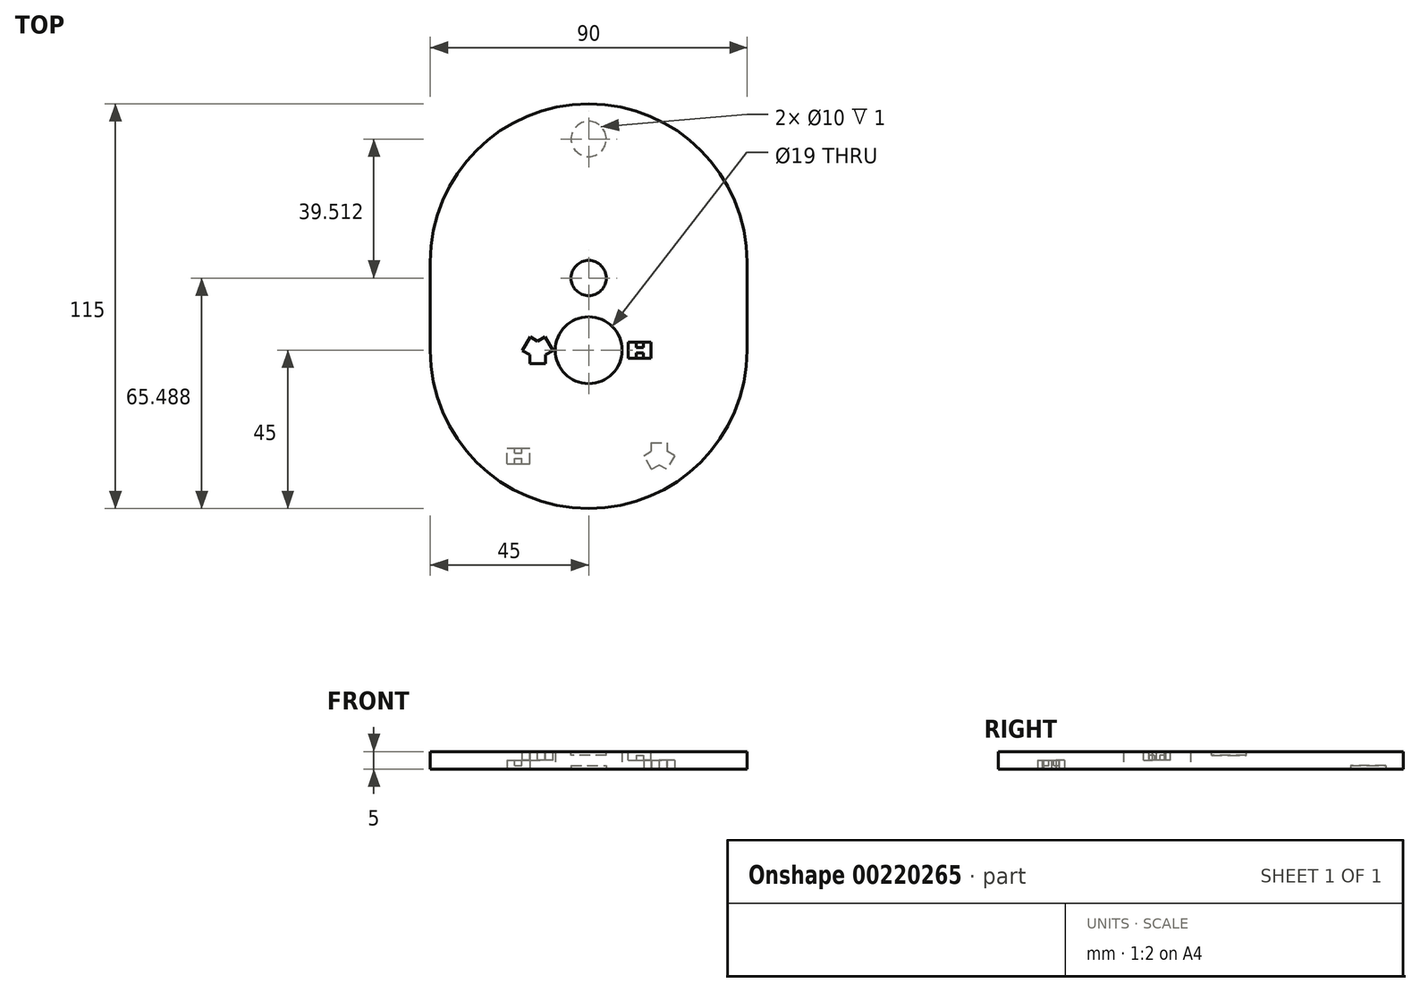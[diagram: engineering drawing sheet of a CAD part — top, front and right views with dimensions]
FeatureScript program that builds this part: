
annotation { "Feature Type Name" : "Feature", "Feature Type Description" : "" }
export const myFeature = defineFeature(function(context is Context, id is Id, definition is map)
    precondition{}
    {
        {
            var Q0;
            Q0=qCreatedBy(makeId("Top.planeOp"),FACE);
            var sketch = newSketch(context, id + "F0", { "sketchPlane" : qUnion([Q0])});
            skArc(sketch, "E0", {"start": v(-45, 0) * mm, "mid": v(0, -45) * mm, "end": v(45, 0) * mm});
            skLineSegment(sketch, "E1", {"start": v(-45, 0) * mm, "end": v(-45, 70) * mm});
            skLineSegment(sketch, "E2", {"start": v(-45, 70) * mm, "end": v(45, 70) * mm});
            skLineSegment(sketch, "E3", {"start": v(45, 70) * mm, "end": v(45, 0) * mm});
            skSolve(sketch);
        }
        {
            var Q0;
            Q0=qSketchRegion(id+"F0",true);
            extrude(context, id + "F1", {"entities" : qUnion([Q0]), "depth" : 5 * mm});
        }
        {
            var Q0;
            Q0=makeQuery(id+"F1.opExtrude","CAP_FACE",FACE,{"disambiguationData":[OSD([sQuery(id+"F0.wireOp",EDGE,"E0")])],"isStart":false});
            var sketch = newSketch(context, id + "F2", { "sketchPlane" : qUnion([Q0])});
            skPoint(sketch, "E4", {"position": v(-14.5, 0) * mm});
            skLineSegment(sketch, "E5", {"start": v(-16.62, 3.83) * mm, "end": v(-18.87, -0.07) * mm});
            skLineSegment(sketch, "E6", {"start": v(-16.75, -3.75) * mm, "end": v(-12.25, -3.75) * mm});
            skLineSegment(sketch, "E7", {"start": v(-10.12, -0.07) * mm, "end": v(-12.37, 3.83) * mm});
            skLineSegment(sketch, "E8", {"start": v(-18.87, -0.07) * mm, "end": v(-16.75, -1.3) * mm});
            skLineSegment(sketch, "E9", {"start": v(-16.62, 3.83) * mm, "end": v(-14.5, 2.6) * mm});
            skLineSegment(sketch, "E10", {"start": v(-16.75, -3.75) * mm, "end": v(-16.75, -1.3) * mm});
            skLineSegment(sketch, "E11", {"start": v(-12.25, -3.75) * mm, "end": v(-12.25, -1.3) * mm});
            skLineSegment(sketch, "E12", {"start": v(-12.37, 3.83) * mm, "end": v(-14.5, 2.6) * mm});
            skLineSegment(sketch, "E13", {"start": v(-10.12, -0.07) * mm, "end": v(-12.25, -1.3) * mm});
            skPoint(sketch, "E14.orphan", {"position": v(-8, -3.75) * mm});
            skPoint(sketch, "E15.orphan", {"position": v(-14.5, 7.5) * mm});
            skPoint(sketch, "E16.orphan", {"position": v(-21, -3.75) * mm});
            skSolve(sketch);
        }
        {
            var Q0;
            Q0=qSketchRegion(id+"F2",true);
            extrude(context, id + "F3", {"entities" : qUnion([Q0]), "operationType" : NewBodyOperationType.REMOVE, "oppositeDirection" : true, "depth" : 2.5 * mm});
        }
        {
            var Q0;
            Q0=makeQuery(id+"F1.opExtrude","CAP_FACE",FACE,{"disambiguationData":[OSD([sQuery(id+"F0.wireOp",EDGE,"E0")])],"isStart":false});
            var sketch = newSketch(context, id + "F4", { "sketchPlane" : qUnion([Q0])});
            skPoint(sketch, "E17", {"position": v(14.5, 0) * mm});
            skLineSegment(sketch, "E18.bottom", {"start": v(11.25, 2.25) * mm, "end": v(17.75, 2.25) * mm});
            skLineSegment(sketch, "E18.top", {"start": v(11.25, -2.25) * mm, "end": v(17.75, -2.25) * mm});
            skLineSegment(sketch, "E18.left", {"start": v(11.25, 2.25) * mm, "end": v(11.25, -2.25) * mm});
            skLineSegment(sketch, "E18.right", {"start": v(17.75, 2.25) * mm, "end": v(17.75, -2.25) * mm});
            skSolve(sketch);
        }
        {
            var Q0;
            Q0=qSketchRegion(id+"F4",true);
            extrude(context, id + "F5", {"entities" : qUnion([Q0]), "operationType" : NewBodyOperationType.REMOVE, "oppositeDirection" : true, "depth" : 2.5 * mm});
        }
        {
            var Q0;
            Q0=makeQuery(id+"F5.boolean.opBoolean","COPY",FACE,{"derivedFrom":makeQuery(id+"F5.opExtrude","CAP_FACE",FACE,{"disambiguationData":[OSD([sQuery(id+"F4.wireOp",EDGE,"E18.bottom"),sQuery(id+"F4.wireOp",EDGE,"E18.top"),sQuery(id+"F4.wireOp",EDGE,"E18.left"),sQuery(id+"F4.wireOp",EDGE,"E18.right")])],"isStart":false})});
            var sketch = newSketch(context, id + "F6", { "sketchPlane" : qUnion([Q0])});
            skLineSegment(sketch, "E19.bottom", {"start": v(13.5, 2.25) * mm, "end": v(15.5, 2.25) * mm});
            skLineSegment(sketch, "E19.top", {"start": v(13.5, -2.25) * mm, "end": v(15.5, -2.25) * mm});
            skLineSegment(sketch, "E19.left", {"start": v(13.5, 2.25) * mm, "end": v(13.5, 0.75) * mm});
            skLineSegment(sketch, "E19.right", {"start": v(15.5, 2.25) * mm, "end": v(15.5, 0.75) * mm});
            skLineSegment(sketch, "E20", {"start": v(13.5, 0.75) * mm, "end": v(15.5, 0.75) * mm});
            skLineSegment(sketch, "E21", {"start": v(13.5, -0.75) * mm, "end": v(15.5, -0.75) * mm});
            skLineSegment(sketch, "E22.trimOffspring", {"start": v(13.5, -0.75) * mm, "end": v(13.5, -2.25) * mm});
            skLineSegment(sketch, "E23.trimOffspring", {"start": v(15.5, -0.75) * mm, "end": v(15.5, -2.25) * mm});
            skSolve(sketch);
        }
        {
            var Q0;
            Q0=qSketchRegion(id+"F6",true);
            extrude(context, id + "F7", {"entities" : qUnion([Q0]), "operationType" : NewBodyOperationType.ADD, "depth" : 1.5 * mm});
        }
        {
            var Q0;
            Q0=makeQuery(id+"F1.opExtrude","CAP_FACE",FACE,{"disambiguationData":[OSD([sQuery(id+"F0.wireOp",EDGE,"E0")])],"isStart":false});
            var sketch = newSketch(context, id + "F8", { "sketchPlane" : qUnion([Q0])});
            skPoint(sketch, "E24", {"position": v(0, 20.49) * mm});
            skPoint(sketch, "E25", {"position": v(-14.5, 0) * mm});
            skCircle(sketch, "E26", {"center": v(0, 20.49) * mm, "radius": 5 * mm});
            skSolve(sketch);
        }
        {
            var Q0;
            Q0=qSketchRegion(id+"F8",true);
            extrude(context, id + "F9", {"entities" : qUnion([Q0]), "operationType" : NewBodyOperationType.REMOVE, "oppositeDirection" : true, "depth" : 1 * mm});
        }
        {
            var Q0;
            Q0=makeQuery(id+"F1.opExtrude","CAP_FACE",FACE,{"disambiguationData":[OSD([sQuery(id+"F0.wireOp",EDGE,"E0")])],"isStart":true});
            var sketch = newSketch(context, id + "F10", { "sketchPlane" : qUnion([Q0])});
            skCircle(sketch, "E27", {"center": v(0, 0) * mm, "radius": 9.5 * mm});
            skSolve(sketch);
        }
        {
            var Q0;
            Q0=qSketchRegion(id+"F10",true);
            extrude(context, id + "F11", {"entities" : qUnion([Q0]), "operationType" : NewBodyOperationType.REMOVE, "oppositeDirection" : true, "depth" : 10 * mm});
        }
        {
            var Q0;
            Q0=makeQuery(id+"F1.opExtrude","CAP_FACE",FACE,{"disambiguationData":[OSD([sQuery(id+"F0.wireOp",EDGE,"E0")])],"isStart":true});
            var sketch = newSketch(context, id + "F12", { "sketchPlane" : qUnion([Q0])});
            skCircle(sketch, "E28", {"center": v(0, -60) * mm, "radius": 5 * mm});
            skSolve(sketch);
        }
        {
            var Q0;
            Q0=makeQuery(id+"F1.opExtrude","CAP_FACE",FACE,{"disambiguationData":[OSD([sQuery(id+"F0.wireOp",EDGE,"E0"),sQuery(id+"F0.wireOp",EDGE,"E1"),sQuery(id+"F0.wireOp",EDGE,"E2"),sQuery(id+"F0.wireOp",EDGE,"E3")])],"isStart":true});
            var sketch = newSketch(context, id + "F13", { "sketchPlane" : qUnion([Q0])});
            skPoint(sketch, "E29", {"position": v(20, 30) * mm});
            skLineSegment(sketch, "E30", {"start": v(17.88, 33.83) * mm, "end": v(15.63, 29.93) * mm});
            skLineSegment(sketch, "E31", {"start": v(17.75, 26.25) * mm, "end": v(22.25, 26.25) * mm});
            skLineSegment(sketch, "E32", {"start": v(24.37, 29.93) * mm, "end": v(22.12, 33.83) * mm});
            skLineSegment(sketch, "E33", {"start": v(15.62, 29.93) * mm, "end": v(17.75, 28.7) * mm});
            skLineSegment(sketch, "E34", {"start": v(17.87, 33.83) * mm, "end": v(20, 32.6) * mm});
            skLineSegment(sketch, "E35", {"start": v(17.75, 26.25) * mm, "end": v(17.75, 28.7) * mm});
            skLineSegment(sketch, "E36", {"start": v(22.25, 26.25) * mm, "end": v(22.25, 28.7) * mm});
            skLineSegment(sketch, "E37", {"start": v(22.12, 33.83) * mm, "end": v(20, 32.6) * mm});
            skLineSegment(sketch, "E38", {"start": v(24.38, 29.93) * mm, "end": v(22.25, 28.7) * mm});
            skPoint(sketch, "E39.orphan", {"position": v(26.5, 26.25) * mm});
            skPoint(sketch, "E40.orphan", {"position": v(20, 37.5) * mm});
            skPoint(sketch, "E41.orphan", {"position": v(13.5, 26.25) * mm});
            skSolve(sketch);
        }
        {
            var Q0;
            Q0=qSketchRegion(id+"F13",true);
            extrude(context, id + "F14", {"entities" : qUnion([Q0]), "operationType" : NewBodyOperationType.REMOVE, "oppositeDirection" : true, "depth" : 2.5 * mm});
        }
        {
            var Q0;
            Q0=qSketchRegion(id+"F12",true);
            extrude(context, id + "F15", {"entities" : qUnion([Q0]), "operationType" : NewBodyOperationType.REMOVE, "oppositeDirection" : true, "depth" : 1 * mm});
        }
        {
            var Q0;
            Q0=makeQuery(id+"F1.opExtrude","CAP_FACE",FACE,{"disambiguationData":[OSD([sQuery(id+"F0.wireOp",EDGE,"E0"),sQuery(id+"F0.wireOp",EDGE,"E1"),sQuery(id+"F0.wireOp",EDGE,"E2"),sQuery(id+"F0.wireOp",EDGE,"E3")])],"isStart":true});
            var sketch = newSketch(context, id + "F16", { "sketchPlane" : qUnion([Q0])});
            skPoint(sketch, "E42", {"position": v(-20, 30) * mm});
            skLineSegment(sketch, "E43.bottom", {"start": v(-23.25, 32.25) * mm, "end": v(-16.75, 32.25) * mm});
            skLineSegment(sketch, "E43.top", {"start": v(-23.25, 27.75) * mm, "end": v(-16.75, 27.75) * mm});
            skLineSegment(sketch, "E43.left", {"start": v(-23.25, 32.25) * mm, "end": v(-23.25, 27.75) * mm});
            skLineSegment(sketch, "E43.right", {"start": v(-16.75, 32.25) * mm, "end": v(-16.75, 27.75) * mm});
            skSolve(sketch);
        }
        {
            var Q0;
            Q0=qSketchRegion(id+"F16",true);
            extrude(context, id + "F17", {"entities" : qUnion([Q0]), "operationType" : NewBodyOperationType.REMOVE, "oppositeDirection" : true, "depth" : 2.5 * mm});
        }
        {
            var Q0;
            Q0=makeQuery(id+"F17.boolean.opBoolean","COPY",FACE,{"derivedFrom":makeQuery(id+"F17.opExtrude","CAP_FACE",FACE,{"disambiguationData":[OSD([sQuery(id+"F16.wireOp",EDGE,"E43.bottom"),sQuery(id+"F16.wireOp",EDGE,"E43.top"),sQuery(id+"F16.wireOp",EDGE,"E43.left"),sQuery(id+"F16.wireOp",EDGE,"E43.right")])],"isStart":false})});
            var sketch = newSketch(context, id + "F18", { "sketchPlane" : qUnion([Q0])});
            skLineSegment(sketch, "E44.bottom", {"start": v(-21, 32.25) * mm, "end": v(-19, 32.25) * mm});
            skLineSegment(sketch, "E44.top", {"start": v(-21, 27.75) * mm, "end": v(-19, 27.75) * mm});
            skLineSegment(sketch, "E44.left", {"start": v(-21, 32.25) * mm, "end": v(-21, 30.75) * mm});
            skLineSegment(sketch, "E44.right", {"start": v(-19, 32.25) * mm, "end": v(-19, 30.75) * mm});
            skLineSegment(sketch, "E45", {"start": v(-21, 30.75) * mm, "end": v(-19, 30.75) * mm});
            skLineSegment(sketch, "E46", {"start": v(-21, 29.25) * mm, "end": v(-19, 29.25) * mm});
            skLineSegment(sketch, "E47.trimOffspring", {"start": v(-21, 29.25) * mm, "end": v(-21, 27.75) * mm});
            skLineSegment(sketch, "E48.trimOffspring", {"start": v(-19, 29.25) * mm, "end": v(-19, 27.75) * mm});
            skSolve(sketch);
        }
        {
            var Q0;
            Q0=qSketchRegion(id+"F18",true);
            extrude(context, id + "F19", {"entities" : qUnion([Q0]), "operationType" : NewBodyOperationType.ADD, "depth" : 1.5 * mm});
        }
        {
            var Q0;
            Q0=makeQuery(id+"F1.opExtrude","SWEPT_EDGE",EDGE,{"disambiguationData":[OSD([sQuery(id+"F0.wireOp",EDGE,"E1"),sQuery(id+"F0.wireOp",EDGE,"E2")])]});
            var Q1;
            Q1=makeQuery(id+"F1.opExtrude","SWEPT_EDGE",EDGE,{"disambiguationData":[OSD([sQuery(id+"F0.wireOp",EDGE,"E2"),sQuery(id+"F0.wireOp",EDGE,"E3")])]});
            fillet(context, id + "F20", {"entities" : qUnion([Q0, Q1]), "radius" : 45 * mm, "tangentPropagation" : true, "allowEdgeOverflow" : false});
        }
    });
